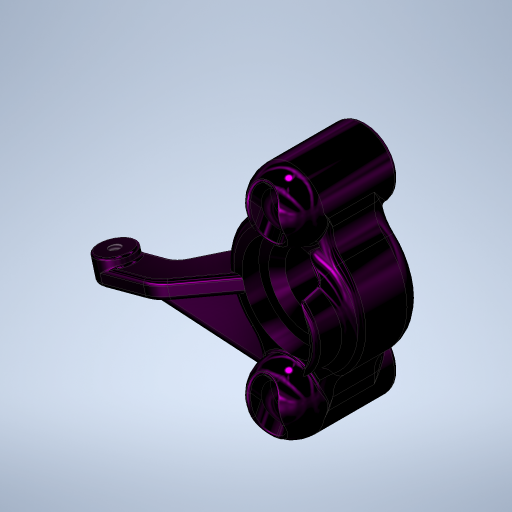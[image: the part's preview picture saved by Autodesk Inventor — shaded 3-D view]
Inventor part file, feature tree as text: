
AUTODESK INVENTOR PART (.ipt)
format: ipt  version: 2023.1 (Build 271208000, 208)  size: 1,274,368 bytes
history: native  units: in
note: dims shown in document units (in); Inventor stores cm internally (conversion verified against a paired STEP export)
features: fillet x18, sketch x13, extrude x9, projected_geometry x6, plane x4, revolve x3, other x3, chamfer x2, thread x2, mirror x1, hole x1, rib x1, draft x1
ambient origin geometry x8: Origin, YZ Plane, XZ Plane, XY Plane, X Axis, Y Axis, Z Axis, Center Point
bodies: Solid1 (feature_tree)
feature tree (64):
  extrude  "Extrusion1"  Depth=0.5in
  fillet  "Fillet1"  Radius=0.5in
  revolve  "Revolution1"  [1 undecoded]
  mirror  "Mirror1"
  extrude  "Extrusion2"  TaperAngle=90.0deg  [1 undecoded]
  extrude  "Extrusion3"  Depth=0.125in TaperAngle=0.0deg
  plane  "Work Plane1"
  plane  "Work Plane3"
  extrude  "Extrusion4"  Depth=0.1875in TaperAngle=0.0deg
  revolve  "Revolution2"  Angle=15.0deg
  revolve  "Revolution3"  [1 undecoded]
  fillet  "Fillet2"  Radius=0.215in
  extrude  "Extrusion5"  Depth=0.215in
  chamfer  "Chamfer1"  Distance=0.0625in
  extrude  "Extrusion6"  Depth=0.475in
  fillet  "Fillet3"  Radius=0.0625in
  fillet  "Fillet4"  Radius=0.015in
  fillet  "Fillet5"  Radius=0.0625in
  fillet  "Fillet6"  Radius=0.015in
  chamfer  "Chamfer2"  Distance=0.0625in Angle=45.0deg
  thread  "Thread1"  [1 undecoded]
  thread  "Thread2"  [1 undecoded]
  fillet  "Fillet7"  Radius=0.125in
  fillet  "Fillet8"  Radius=0.032in
  fillet  "Fillet9"  Radius=0.032in
  extrude  "Extrusion7"  Depth=0.135in
  fillet  "Fillet10"  Radius=1.2in
  extrude  "Extrusion8"  Depth=0.15in
  fillet  "Fillet11"  [1 undecoded]
  hole  "Hole1"  [1 undecoded]
  fillet  "Fillet12"  Radius=0.25in
  plane  "Work Plane4"
  rib  "Rib1"
  fillet  "Fillet13"  Radius=0.125in
  extrude  "Extrusion9"  Depth=0.0625in TaperAngle=0.0deg
  draft  "FaceDraft1"
  fillet  "Fillet14"  Radius=0.032in
  fillet  "Fillet15"  Radius=0.015in
  fillet  "Fillet16"  Radius=0.1in
  fillet  "Fillet17"  Radius=0.05in
  fillet  "Fillet18"  Radius=0.315in
  sketch  "Sketch1"  dims[d0=1.7625in d1=0.5in d3=0.5in]
  sketch  "Sketch2"  dims[d4=0.5625in d5=0.0in d6=0.25in]
  sketch  "Sketch3"  dims[d8=0.325in d9=90.0deg]
  sketch  "Sketch4"  dims[d10=0.75in d11=0.125in d12=0.0in]
  other  "Work Axis1"
  other  "Work Axis2"
  plane  "Work Plane2"
  other  "Work Axis3"
  sketch  "Sketch5"  dims[d13=0.5in d14=0.1875in d15=0.0in]
  sketch  "Sketch6"  dims[d16=15.0deg d17=15.0deg]
  sketch  "Sketch7"  dims[d18=0.0in d19=0.0in d20=0.0in d21=0.215in]
  sketch  "Sketch8"  dims[d22=0.6871in d23=0.215in]
  sketch  "Sketch9"  dims[d24=0.6871in]
  sketch  "Sketch10"  dims[d25=0.1in d26=0.0625in d27=0.0in]
  sketch  "Sketch11"  dims[d28=0.015in d29=0.125in d30=45.0deg d31=0.475in d32=0.0625in d33=0.0in d34=0.015in d35=0.0625in d36=0.015in]
  sketch  "Sketch12"  dims[d37=0.014in d38=0.0625in d39=0.125in d40=45.0deg d41=0.315in d42=0.0in d43=0.315in d44=0.0in d45=0.125in d46=0.032in d47=0.032in]
  sketch  "Sketch14"  dims[d48=0.3779in d49=0.135in d50=1.2in d51=0.15in d52=15.0deg d53=0.125in d54=0.0in d55=0.25in d56=0.125in d57=0.0625in d58=0.0in d59=0.032in d60=0.0849in d61=0.224in d62=0.375in d63=0.25in d64=0.5635in d65=0.349in d66=0.8108in d67=0.015in d68=0.1in d69=0.1in d70=0.0in d71=0.0in d72=0.1in d73=0.1in d74=0.05in d75=0.315in d76=0.25in d77=0.0in d78=0.0172in d79=0.125in d80=0.032in d81=0.015in d82=0.015in d83=0.015in]
  projected_geometry  "Project Cut Edges1"
  projected_geometry  "Project Cut Edges2"
  projected_geometry  "Project Cut Edges3"
  projected_geometry  "Project Cut Edges4"
  projected_geometry  "Project Cut Edges5"
  projected_geometry  "Project Cut Edges6"
note: 7 required parameter values undecoded (feature->parameter linkage not recoverable at this tier; creation-order binding heuristic only, values carry confidence <= 0.55)